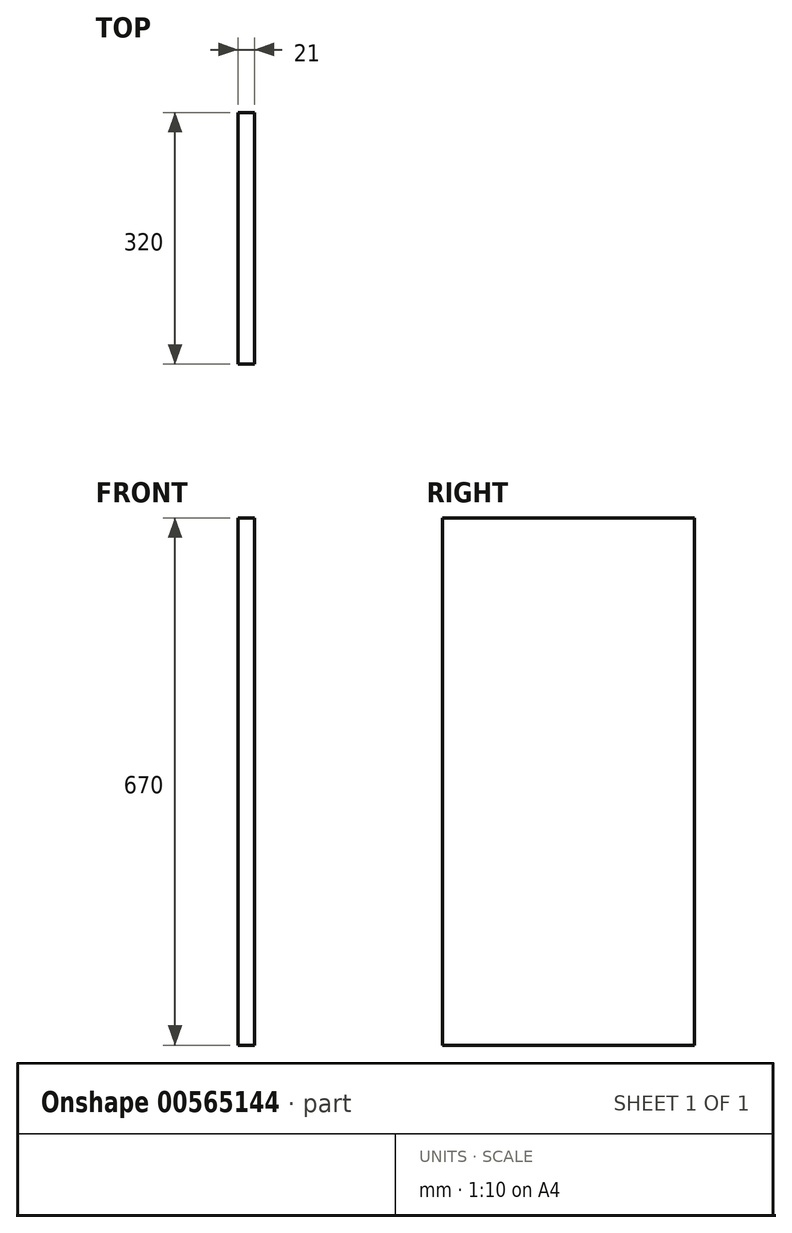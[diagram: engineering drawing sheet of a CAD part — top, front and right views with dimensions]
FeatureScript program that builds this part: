
annotation { "Feature Type Name" : "Feature", "Feature Type Description" : "" }
export const myFeature = defineFeature(function(context is Context, id is Id, definition is map)
    precondition{}
    {
        {
            var Q0;
            Q0=qCreatedBy(makeId("Right.planeOp"),FACE);
            var sketch = newSketch(context, id + "F0", { "sketchPlane" : qUnion([Q0])});
            skLineSegment(sketch, "E0.bottom", {"start": v(160, 335) * mm, "end": v(-160, 335) * mm});
            skLineSegment(sketch, "E0.top", {"start": v(160, -335) * mm, "end": v(-160, -335) * mm});
            skLineSegment(sketch, "E0.left", {"start": v(160, 335) * mm, "end": v(160, -335) * mm});
            skLineSegment(sketch, "E0.right", {"start": v(-160, 335) * mm, "end": v(-160, -335) * mm});
            skPoint(sketch, "E0.middle", {"position": v(0, 0) * mm});
            skSolve(sketch);
        }
        {
            var Q0;
            Q0=makeQuery(id+"F0.imprint","IMPRINT",FACE,{"disambiguationData":[TD([[makeQuery(id+"F0.imprint","IMPRINT",EDGE,{"derivedFrom":sQuery(id+"F0.wireOp",EDGE,"E0.bottom")}),1.0]])]});
            extrude(context, id + "F1", {"entities" : qUnion([Q0]), "depth" : 21 * mm, "offsetDistance" : 25 * mm});
        }
    });
